FCSTD DOCUMENT  (FreeCAD 1.1R20260325 (Git shallow))
Label: FujiXE-design
License: Creative Commons Attribution 4.0
objects: Sketcher::SketchObject×9, Image::ImagePlane×4, App::Point×1, App::VarSet×1, PartDesign::Body×1
note: 19 computed .brp shape members not serialized (recipe doc carries the construction recipe); baked Part::Feature solids carry a one-line shape summary decoded from their .brp

FEATURE [App::Point] Origin001
  Role = Origin
FEATURE [App::VarSet] VarSet  label="Data"
  AVAngle = 38
  Height = 4.8
  MidGlyphWidth = 0.66
  MidHorizontalBarY = 2.2
  Thickness = 0.8
  ThinLetterWidth = 3.5
  TopOfA = 1
  Width = 3.95
FEATURE [Sketcher::SketchObject] Sketch  label="A"
  ArcFitTolerance = 1e-06
  AttachmentSupport = -> [Origin]
  ExternalTypes = [0]
  FullyConstrained = false
  MakeInternals = false
  MapMode = 5
  _ExternalGeoVersion = 1
  expr: Constraints[29] = <<Data>>.TopOfA
  expr: Constraints[30] = <<Data>>.AVAngle
  expr: Constraints[32] = <<Data>>.MidGlyphWidth
  expr: Constraints[36] = <<Data>>.Thickness
  expr: Constraints[37] = <<Data>>.Height
  sketch-geometry (17):
    g0: LineSegment StartX=23.478 StartY=44.0896 StartZ=0 EndX=25.1308 EndY=48.8896 EndZ=0
    g1: LineSegment StartX=25.1308 StartY=48.8896 StartZ=0 EndX=26.1308 EndY=48.8896 EndZ=0
    g2: LineSegment StartX=26.1308 StartY=48.8896 StartZ=0 EndX=27.7835 EndY=44.0896 EndZ=0
    g3: LineSegment StartX=27.7835 StartY=44.0896 StartZ=0 EndX=26.9374 EndY=44.0896 EndZ=0
    g4: LineSegment StartX=26.9374 StartY=44.0896 StartZ=0 EndX=26.5862 EndY=45.1096 EndZ=0
    g5: LineSegment StartX=26.5862 StartY=45.1096 StartZ=0 EndX=24.6753 EndY=45.1096 EndZ=0
    g6: LineSegment StartX=24.6753 StartY=45.1096 StartZ=0 EndX=24.3241 EndY=44.0896 EndZ=0
    g7: LineSegment StartX=24.3241 StartY=44.0896 StartZ=0 EndX=23.478 EndY=44.0896 EndZ=0
    g8: LineSegment StartX=24.9026 StartY=45.7696 StartZ=0 EndX=25.6308 EndY=47.8845 EndZ=0
    g9: LineSegment StartX=25.6308 StartY=47.8845 StartZ=0 EndX=26.359 EndY=45.7696 EndZ=0
    g10: LineSegment StartX=26.359 StartY=45.7696 StartZ=0 EndX=24.9026 EndY=45.7696 EndZ=0
    g11: GeomPoint [constr] X=25.6308 Y=45.7696 Z=0
    g12: GeomPoint [constr] X=25.6308 Y=48.8896 Z=0
    g13: LineSegment [constr] StartX=24.6753 StartY=45.1096 StartZ=0 EndX=23.9189 EndY=45.37 EndZ=0
    g14: GeomPoint [constr] X=25.6308 Y=45.1096 Z=0
    g15: GeomPoint [constr] X=25.6308 Y=44.0896 Z=0
    g16: GeomPoint [constr] X=25.6308 Y=45.4396 Z=0
  constraints (39):
    c: Coincident(g0,g1)
    c: Horizontal(g1)
    c: Coincident(g1,g2)
    c: Coincident(g2,g3)
    c: Horizontal(g3)
    c: Coincident(g3,g4)
    c: Coincident(g4,g5)
    c: Horizontal(g5)
    c: Coincident(g5,g6)
    c: Coincident(g6,g7)
    c: Coincident(g7,g0)
    c: Horizontal(g7)
    c: Horizontal(g6,g3)
    c: Coincident(g8,g9)
    c: Coincident(g9,g10)
    c: Coincident(g10,g8)
    c: Horizontal(g10)
    c: PointOnObject(g4,g9)
    c: PointOnObject(g5,g8)
    c: Parallel(g0,g6)
    c: Parallel(g4,g2)
    c: Symmetric(g10,g10,g11)
    c: Vertical(g8,g11)
    c: Symmetric(g1,g1,g12)
    c: Vertical(g8,g12)
    c: Equal(g7,g3)
    c: Coincident(g13,g5)
    c: PointOnObject(g13,g0)
    c: Perpendicular(g0,g13)
    c: DistanceX(g1,g1) = 1
    c: Angle(g0,g2) = 0.663225
    c: Symmetric(g5,g5,g14)
    c: DistanceY(g14,g11) = 0.66
    c: Symmetric(g6,g3,g15)
    c: Symmetric(g11,g14,g16)
    c: DistanceY(g15,g16) = 1.35
    c: Distance(g13) = 0.8
    c: DistanceY(g2,g1) = 4.8
    c: Parallel(g0,g8)
FEATURE [Sketcher::SketchObject] Sketch001  label="S"
  ArcFitTolerance = 1e-06
  AttachmentSupport = -> [Sketch]
  ExternalTypes = [0]
  FullyConstrained = false
  MakeInternals = false
  MapMode = 2
  _ExternalGeoVersion = 1
  sketch-geometry (50):
    g0: LineSegment StartX=8.4208 StartY=47.4982 StartZ=0 EndX=9.33017 EndY=47.532 EndZ=0
    g1: LineSegment StartX=5.53142 StartY=45.4144 StartZ=0 EndX=6.4408 EndY=45.4482 EndZ=0
    g2-g12: Circle [constr] x11 (B-spline internal-alignment scaffolding for g13; pole/knot coordinates omitted)
    g13: BSplineCurve PolesCount=11 KnotsCount=9 Degree=3 IsPeriodic=0
    g14-g22: GeomPoint [constr] x9 (B-spline internal-alignment scaffolding for g13; pole/knot coordinates omitted)
    g23-g36: Circle [constr] x14 (B-spline internal-alignment scaffolding for g37; pole/knot coordinates omitted)
    g37: BSplineCurve PolesCount=14 KnotsCount=12 Degree=3 IsPeriodic=0
    g38-g49: GeomPoint [constr] x12 (B-spline internal-alignment scaffolding for g37; pole/knot coordinates omitted)
  constraints (37):
    c: DistanceY(g1,g0) = 2.05
    c: DistanceX(g1,g0) = 1.98
    c: Equal(g1,g0)
    c: Parallel(g1,g0)
    c: Weight(g2) = 1
    c: Equal(g2, g3-g12) x10
    c: InternalAlignment(g2-g12 -> g13) x11
    c: InternalAlignment(g14-g22 -> g13) x9
    c: Coincident(g2,g0)
    c: Coincident(g12,g1)
    c: Horizontal(g19,g8)
    c: Vertical(g10,g21)
    c: DistanceY(g18,g0) = 0.91
    c: DistanceX(g18,g0) = 0.61
    c: DistanceX(g17,g0) = 2.19
    c: DistanceY(g17,g0) = 0.55
    c: DistanceX(g16,g13) = 1.82
    c: DistanceY(g13,g16) = 0.11
    c: DistanceY(g0,g3) = 0.55
    c: DistanceX(g3,g0) = 1
    c: DistanceY(g0,g15) = 0.64
    c: DistanceX(g15,g0) = 1.99
    c: DistanceY(g20,g0) = 3.2
    c: DistanceX(g20,g0) = 0.46
    c: DistanceX(g21,g0) = 2.21
    c: DistanceY(g21,g0) = 3.61
    c: DistanceY(g19,g0) = 2.01
    c: DistanceX(g0,g19) = 0.12
    c: Distance(g0) = 0.91
    c: Weight(g23) = 1
    c: Equal(g23, g24-g36) x13
    c: InternalAlignment(g23-g36 -> g37) x14
    c: InternalAlignment(g38-g49 -> g37) x12
    c: Coincident(g23,g0)
    c: PointOnObject(g25,g24)
    c: PointOnObject(g28,g27)
    c: Coincident(g36,g1)
FEATURE [Sketcher::SketchObject] Sketch002  label="Z"
  ArcFitTolerance = 1e-06
  AttachmentSupport = -> [Origin]
  ExternalTypes = [0]
  FullyConstrained = false
  MakeInternals = false
  MapMode = 5
  _ExternalGeoVersion = 1
  expr: Constraints[20] = <<Data>>.Height
  expr: Constraints[24] = <<Data>>.Width
  expr: Constraints[29] = <<Data>>.Thickness
  sketch-geometry (11):
    g0: LineSegment StartX=-9.16198 StartY=26.3031 StartZ=0 EndX=-9.16198 EndY=27.1031 EndZ=0
    g1: LineSegment StartX=-9.16198 StartY=27.1031 StartZ=0 EndX=-5.21198 EndY=27.1031 EndZ=0
    g2: LineSegment StartX=-5.21198 StartY=27.1031 StartZ=0 EndX=-5.21198 EndY=26.3031 EndZ=0
    g3: LineSegment StartX=-5.21198 StartY=26.3031 StartZ=0 EndX=-7.97324 EndY=23.1031 EndZ=0
    g4: LineSegment StartX=-7.97324 StartY=23.1031 StartZ=0 EndX=-5.21198 EndY=23.1031 EndZ=0
    g5: LineSegment StartX=-5.21198 StartY=23.1031 StartZ=0 EndX=-5.21198 EndY=22.3031 EndZ=0
    g6: LineSegment StartX=-5.21198 StartY=22.3031 StartZ=0 EndX=-9.16198 EndY=22.3031 EndZ=0
    g7: LineSegment StartX=-9.16198 StartY=22.3031 StartZ=0 EndX=-9.16198 EndY=23.1031 EndZ=0
    g8: LineSegment StartX=-9.16198 StartY=23.1031 StartZ=0 EndX=-6.40072 EndY=26.3031 EndZ=0
    g9: LineSegment StartX=-6.40072 StartY=26.3031 StartZ=0 EndX=-9.16198 EndY=26.3031 EndZ=0
    g10: LineSegment [constr] StartX=-7.97324 StartY=23.1031 StartZ=0 EndX=-8.65463 EndY=23.6911 EndZ=0
  constraints (31):
    c: Vertical(g0)
    c: Coincident(g0,g1)
    c: Horizontal(g1)
    c: Coincident(g1,g2)
    c: Vertical(g2)
    c: Coincident(g2,g3)
    c: Coincident(g3,g4)
    c: Horizontal(g4)
    c: Coincident(g4,g5)
    c: Vertical(g5)
    c: Coincident(g5,g6)
    c: Horizontal(g6)
    c: Coincident(g6,g7)
    c: Vertical(g7)
    c: Coincident(g7,g8)
    c: Coincident(g8,g9)
    c: Coincident(g9,g0)
    c: Horizontal(g9)
    c: Vertical(g2,g4)
    c: Vertical(g0,g7)
    c: DistanceY(g6,g0) = 4.8
    c: Horizontal(g8,g2)
    c: Horizontal(g7,g3)
    c: Parallel(g8,g3)
    c: DistanceX(g6,g6) = 3.95
    c: Coincident(g10,g3)
    c: PointOnObject(g10,g8)
    c: Perpendicular(g8,g10)
    c: Distance(g10) = 0.9
    c: DistanceY(g5,g5) = 0.8
    c: Equal(g5,g0)
FEATURE [Sketcher::SketchObject] Sketch003  label="X"
  ArcFitTolerance = 1e-06
  AttachmentSupport = -> [Sketch002]
  ExternalTypes = [0]
  FullyConstrained = false
  MakeInternals = false
  MapMode = 2
  _ExternalGeoVersion = 1
  expr: Constraints[16] = <<Data>>.Height
  sketch-geometry (13):
    g0: LineSegment StartX=8.97005 StartY=27.4466 StartZ=0 EndX=9.9513 EndY=27.4466 EndZ=0
    g1: LineSegment StartX=9.9513 StartY=27.4466 StartZ=0 EndX=10.8301 EndY=25.9184 EndZ=0
    g2: LineSegment StartX=10.8301 StartY=25.9184 StartZ=0 EndX=11.7088 EndY=27.4466 EndZ=0
    g3: LineSegment StartX=11.7088 StartY=27.4466 StartZ=0 EndX=12.6901 EndY=27.4466 EndZ=0
    g4: LineSegment StartX=12.6901 StartY=27.4466 StartZ=0 EndX=11.3801 EndY=25.1684 EndZ=0
    g5: LineSegment StartX=11.3801 StartY=25.1684 StartZ=0 EndX=12.8301 EndY=22.6466 EndZ=0
    g6: LineSegment StartX=12.8301 StartY=22.6466 StartZ=0 EndX=11.8488 EndY=22.6466 EndZ=0
    g7: LineSegment StartX=11.8488 StartY=22.6466 StartZ=0 EndX=10.8301 EndY=24.4184 EndZ=0
    g8: LineSegment StartX=10.8301 StartY=24.4184 StartZ=0 EndX=9.8113 EndY=22.6466 EndZ=0
    g9: LineSegment StartX=9.8113 StartY=22.6466 StartZ=0 EndX=8.83005 EndY=22.6466 EndZ=0
    g10: LineSegment StartX=8.83005 StartY=22.6466 StartZ=0 EndX=10.2801 EndY=25.1684 EndZ=0
    g11: LineSegment StartX=10.2801 StartY=25.1684 StartZ=0 EndX=8.97005 EndY=27.4466 EndZ=0
    g12: LineSegment [constr] StartX=10.8301 StartY=24.4184 StartZ=0 EndX=10.8301 EndY=25.9184 EndZ=0
  constraints (33):
    c: Horizontal(g0)
    c: Coincident(g0,g1)
    c: Coincident(g1,g2)
    c: Coincident(g2,g3)
    c: Horizontal(g3)
    c: Coincident(g3,g4)
    c: Coincident(g4,g5)
    c: Coincident(g5,g6)
    c: Horizontal(g6)
    c: Coincident(g6,g7)
    c: Coincident(g7,g8)
    c: Coincident(g8,g9)
    c: Horizontal(g9)
    c: Coincident(g9,g10)
    c: Coincident(g10,g11)
    c: Coincident(g11,g0)
    c: DistanceY(g9,g0) = 4.8
    c: Horizontal(g10,g4)
    c: Coincident(g12,g7)
    c: Coincident(g12,g1)
    c: Symmetric(g0,g2,g12)
    c: Symmetric(g8,g6,g12)
    c: Equal(g0,g3)
    c: Equal(g9,g6)
    c: Parallel(g10,g8)
    c: Parallel(g11,g1)
    c: Symmetric(g10,g4,g12)
    c: Parallel(g10,g2)
    c: DistanceX(g0,g3) = 3.72
    c: DistanceX(g9,g5) = 4
    c: DistanceX(g10,g4) = 1.1
    c: DistanceY(g12,g12) = 1.5
    c: Equal(g9,g3)
FEATURE [Sketcher::SketchObject] Sketch004  label="Q"
  ArcFitTolerance = 1e-06
  AttachmentSupport = -> [Origin]
  ExternalTypes = [0]
  FullyConstrained = false
  MakeInternals = false
  MapMode = 5
  _ExternalGeoVersion = 1
  sketch-geometry (19):
    g0: ArcOfEllipse CenterX=1.09175 CenterY=89.324 CenterZ=0 NormalX=0 NormalY=0 NormalZ=1 MajorRadius=1.75 MinorRadius=1.35 AngleXU=-1.5708 StartAngle=0.938881 EndAngle=6.76111
    g1: LineSegment [constr] StartX=1.09175 StartY=87.574 StartZ=0 EndX=1.09175 EndY=91.074 EndZ=0
    g2: LineSegment [constr] StartX=2.44175 StartY=89.324 StartZ=0 EndX=-0.258249 EndY=89.324 EndZ=0
    g3: GeomPoint [constr] X=1.09175 Y=88.2105 Z=0
    g4: GeomPoint [constr] X=1.09175 Y=90.4376 Z=0
    g5: ArcOfEllipse CenterX=1.09175 CenterY=89.324 CenterZ=0 NormalX=0 NormalY=0 NormalZ=1 MajorRadius=2.5 MinorRadius=2.25 AngleXU=-1.5708 StartAngle=0.873331 EndAngle=6.85864
    g6: LineSegment [constr] StartX=1.09175 StartY=86.824 StartZ=0 EndX=1.09175 EndY=91.824 EndZ=0
    g7: LineSegment [constr] StartX=3.34175 StartY=89.324 StartZ=0 EndX=-1.15825 EndY=89.324 EndZ=0
    g8: GeomPoint [constr] X=1.09175 Y=88.2343 Z=0
    g9: GeomPoint [constr] X=1.09175 Y=90.4138 Z=0
    g10: LineSegment StartX=2.18106 StartY=88.2903 StartZ=0 EndX=1.77233 EndY=88.6583 EndZ=0
    g11: LineSegment StartX=1.77233 StartY=88.6583 StartZ=0 EndX=1.30394 EndY=88.1381 EndZ=0
    g12: LineSegment StartX=1.30394 StartY=88.1381 StartZ=0 EndX=1.71267 EndY=87.7701 EndZ=0
    g13: LineSegment StartX=2.31624 StartY=87.2267 StartZ=0 EndX=2.86812 EndY=86.7297 EndZ=0
    g14: LineSegment StartX=2.86812 StartY=86.7297 StartZ=0 EndX=3.33652 EndY=87.2499 EndZ=0
    g15: LineSegment StartX=3.33652 StartY=87.2499 StartZ=0 EndX=2.81631 EndY=87.7183 EndZ=0
    g16: GeomPoint [constr] X=1.53814 Y=88.3982 Z=0
    g17: GeomPoint [constr] X=3.10232 Y=86.9898 Z=0
    g18: LineSegment [constr] StartX=1.53814 StartY=88.3982 StartZ=0 EndX=3.10232 EndY=86.9898 EndZ=0
  constraints (32):
    c: InternalAlignment(g1-g4 -> g0) x4
    c: Vertical(g1)
    c: DistanceY(g1,g1) = 3.5
    c: DistanceX(g2,g2) = 2.7
    c: InternalAlignment(g6-g9 -> g5) x4
    c: Coincident(g5,g0)
    c: Coincident(g10,g0)
    c: Coincident(g10,g11)
    c: Coincident(g11,g12)
    c: Coincident(g12,g0)
    c: Coincident(g13,g5)
    c: Coincident(g13,g14)
    c: Coincident(g14,g15)
    c: Coincident(g15,g5)
    c: Parallel(g12,g10)
    c: Parallel(g13,g15)
    c: Parallel(g10,g15)
    c: Horizontal(g7)
    c: DistanceX(g7,g2) = 0.9
    c: DistanceY(g6,g1) = 0.75
    c: Symmetric(g11,g11,g16)
    c: Symmetric(g14,g14,g17)
    c: Coincident(g18,g16)
    c: Coincident(g18,g17)
    c: Symmetric(g0,g0,g18)
    c: Perpendicular(g10,g11)
    c: Perpendicular(g14,g15)
    c: Equal(g11,g14)
    c: Angle(g1,g18) = 0.837758
    c: Distance(g10) = 0.55
    c: Distance(g15) = 0.7
    c: Distance(g14) = 0.7
FEATURE [Sketcher::SketchObject] Sketch005  label="W"
  ArcFitTolerance = 1e-06
  AttachmentSupport = -> [Sketch004,XY_Plane]
  ExternalTypes = [0]
  FullyConstrained = false
  MakeInternals = false
  MapMode = 2
  _ExternalGeoVersion = 1
  expr: Constraints[21] = <<Data>>.Height
  expr: Constraints[39] = <<Data>>.Thickness
  sketch-geometry (17):
    g0: LineSegment StartX=16.8181 StartY=91.9053 StartZ=0 EndX=18.1042 EndY=87.1053 EndZ=0
    g1: LineSegment StartX=18.1042 StartY=87.1053 StartZ=0 EndX=19.04 EndY=87.1053 EndZ=0
    g2: LineSegment StartX=19.04 StartY=87.1053 StartZ=0 EndX=19.8181 EndY=90.4753 EndZ=0
    g3: LineSegment StartX=19.8181 StartY=90.4753 StartZ=0 EndX=20.5961 EndY=87.1053 EndZ=0
    g4: LineSegment StartX=20.5961 StartY=87.1053 StartZ=0 EndX=21.5319 EndY=87.1053 EndZ=0
    g5: LineSegment StartX=21.5319 StartY=87.1053 StartZ=0 EndX=22.8181 EndY=91.9053 EndZ=0
    g6: LineSegment StartX=22.8181 StartY=91.9053 StartZ=0 EndX=21.9898 EndY=91.9053 EndZ=0
    g7: LineSegment StartX=21.9898 StartY=91.9053 StartZ=0 EndX=21.0596 EndY=88.4335 EndZ=0
    g8: LineSegment StartX=21.0596 StartY=88.4335 StartZ=0 EndX=20.2581 EndY=91.9053 EndZ=0
    g9: LineSegment StartX=20.2581 StartY=91.9053 StartZ=0 EndX=19.3781 EndY=91.9053 EndZ=0
    g10: LineSegment StartX=19.3781 StartY=91.9053 StartZ=0 EndX=18.5765 EndY=88.4335 EndZ=0
    g11: LineSegment StartX=18.5765 StartY=88.4335 StartZ=0 EndX=17.6463 EndY=91.9053 EndZ=0
    g12: LineSegment StartX=17.6463 StartY=91.9053 StartZ=0 EndX=16.8181 EndY=91.9053 EndZ=0
    g13: LineSegment [constr] StartX=19.8181 StartY=87.1053 StartZ=0 EndX=19.8181 EndY=91.9053 EndZ=0
    g14: LineSegment [constr] StartX=18.5721 StartY=87.1053 StartZ=0 EndX=18.5765 EndY=88.4335 EndZ=0
    g15: LineSegment [constr] StartX=21.064 StartY=87.1053 StartZ=0 EndX=21.0596 EndY=88.4335 EndZ=0
    g16: LineSegment [constr] StartX=18.5765 StartY=88.4335 StartZ=0 EndX=17.8038 EndY=88.2265 EndZ=0
  constraints (45):
    c: Coincident(g0,g1)
    c: Coincident(g1,g2)
    c: Coincident(g2,g3)
    c: Coincident(g3,g4)
    c: Horizontal(g4)
    c: Coincident(g4,g5)
    c: Coincident(g5,g6)
    c: Horizontal(g6)
    c: Coincident(g6,g7)
    c: Coincident(g7,g8)
    c: Coincident(g8,g9)
    c: Coincident(g9,g10)
    c: Coincident(g10,g11)
    c: Coincident(g11,g12)
    c: Coincident(g12,g0)
    c: Horizontal(g6,g8)
    c: Horizontal(g3,g1)
    c: Symmetric(g9,g9,g13)
    c: Vertical(g13)
    c: Symmetric(g1,g3,g13)
    c: PointOnObject(g2,g13)
    c: DistanceY(g0,g0) = 4.8
    c: Parallel(g0,g11)
    c: Parallel(g10,g2)
    c: Parallel(g3,g8)
    c: Parallel(g7,g5)
    c: Equal(g1,g4)
    c: Symmetric(g1,g1,g14)
    c: Coincident(g14,g10)
    c: Symmetric(g4,g4,g15)
    c: Coincident(g15,g7)
    c: Coincident(g16,g10)
    c: PointOnObject(g16,g0)
    c: Perpendicular(g0,g16)
    c: Horizontal(g1)
    c: Angle(g2,g3) = 0.453786
    c: Angle(g10,g11) = 0.488692
    c: Horizontal(g12)
    c: Horizontal(g9)
    c: Distance(g16) = 0.8
    c: DistanceX(g0,g5) = 6
    c: Symmetric(g11,g6,g13)
    c: Angle(g7,g8) = 0.488692
    c: DistanceX(g9,g9) = 0.88
    c: DistanceY(g13,g2) = 3.37
FEATURE [Sketcher::SketchObject] Sketch006  label="E"
  ArcFitTolerance = 1e-06
  AttachmentSupport = -> [Origin]
  ExternalTypes = [0]
  FullyConstrained = false
  MakeInternals = false
  MapMode = 5
  _ExternalGeoVersion = 1
  expr: Constraints[26] = <<Data>>.Height
  expr: Constraints[32] = <<Data>>.ThinLetterWidth
  expr: Constraints[33] = <<Data>>.MidHorizontalBarY
  sketch-geometry (12):
    g0: LineSegment StartX=38.8647 StartY=91.9226 StartZ=0 EndX=35.3647 EndY=91.9226 EndZ=0
    g1: LineSegment StartX=35.3647 StartY=91.9226 StartZ=0 EndX=35.3647 EndY=87.1226 EndZ=0
    g2: LineSegment StartX=35.3647 StartY=87.1226 StartZ=0 EndX=38.8647 EndY=87.1226 EndZ=0
    g3: LineSegment StartX=38.8647 StartY=87.1226 StartZ=0 EndX=38.8647 EndY=87.8226 EndZ=0
    g4: LineSegment StartX=38.8647 StartY=87.8226 StartZ=0 EndX=36.2147 EndY=87.8226 EndZ=0
    g5: LineSegment StartX=36.2147 StartY=87.8226 StartZ=0 EndX=36.2147 EndY=89.3226 EndZ=0
    g6: LineSegment StartX=36.2147 StartY=89.3226 StartZ=0 EndX=38.5647 EndY=89.3226 EndZ=0
    g7: LineSegment StartX=38.5647 StartY=89.3226 StartZ=0 EndX=38.5647 EndY=90.0226 EndZ=0
    g8: LineSegment StartX=38.5647 StartY=90.0226 StartZ=0 EndX=36.2147 EndY=90.0226 EndZ=0
    g9: LineSegment StartX=36.2147 StartY=90.0226 StartZ=0 EndX=36.2147 EndY=91.2226 EndZ=0
    g10: LineSegment StartX=36.2147 StartY=91.2226 StartZ=0 EndX=38.8647 EndY=91.2226 EndZ=0
    g11: LineSegment StartX=38.8647 StartY=91.2226 StartZ=0 EndX=38.8647 EndY=91.9226 EndZ=0
  constraints (34):
    c: Horizontal(g0)
    c: Coincident(g0,g1)
    c: Vertical(g1)
    c: Coincident(g1,g2)
    c: Horizontal(g2)
    c: Coincident(g2,g3)
    c: Vertical(g3)
    c: Coincident(g3,g4)
    c: Horizontal(g4)
    c: Coincident(g4,g5)
    c: Vertical(g5)
    c: Coincident(g5,g6)
    c: Horizontal(g6)
    c: Coincident(g6,g7)
    c: Vertical(g7)
    c: Coincident(g7,g8)
    c: Horizontal(g8)
    c: Coincident(g8,g9)
    c: Vertical(g9)
    c: Coincident(g9,g10)
    c: Horizontal(g10)
    c: Coincident(g10,g11)
    c: Coincident(g11,g0)
    c: Vertical(g11)
    c: Equal(g3,g11)
    c: Vertical(g3,g10)
    c: DistanceY(g1,g1) = 4.8
    c: Vertical(g8,g5)
    c: DistanceX(g1,g4) = 0.85
    c: DistanceY(g11,g11) = 0.7
    c: Equal(g7,g11)
    c: DistanceX(g6,g6) = 2.35
    c: DistanceX(g2,g2) = 3.5
    c: DistanceY(g1,g5) = 2.2
FEATURE [Image::ImagePlane] Atari_XE_row_1_caps_reference  label="Atari XE row 1 caps reference"
  XSize = 170.541
  YSize = 65.9345
FEATURE [Image::ImagePlane] Atari_XE_row_2_caps_reference  label="Atari XE row 2 caps reference"
  Placement = pos=(0,46.43,0) rot=(0,0,1;0rad)
  XSize = 141.775
  YSize = 48.4929
FEATURE [Image::ImagePlane] Atari_XE_row_3_caps_reference  label="Atari XE row 3 caps reference"
  Placement = pos=(0,89.74,0) rot=(0,0,1;0rad)
  XSize = 139.065
  YSize = 48.4506
FEATURE [Image::ImagePlane] Atari_XE_row_4_caps_reference  label="Atari XE row 4 caps reference"
  Placement = pos=(0,141.549,0) rot=(0,0,1;0rad)
  XSize = 146.114
  YSize = 55.3298
FEATURE [Sketcher::SketchObject] Sketch007  label="O"
  ArcFitTolerance = 1e-06
  AttachmentSupport = -> [Origin]
  ExternalTypes = [0]
  FullyConstrained = false
  MakeInternals = false
  MapMode = 5
  _ExternalGeoVersion = 1
  sketch-geometry (10):
    g0: Ellipse CenterX=55.1305 CenterY=107.248 CenterZ=0 NormalX=0 NormalY=0 NormalZ=1 MajorRadius=1.74 MinorRadius=1.325 AngleXU=1.5708
    g1: LineSegment [constr] StartX=55.1305 StartY=108.988 StartZ=0 EndX=55.1305 EndY=105.508 EndZ=0
    g2: LineSegment [constr] StartX=53.8055 StartY=107.248 StartZ=0 EndX=56.4555 EndY=107.248 EndZ=0
    g3: GeomPoint [constr] X=55.1305 Y=108.376 Z=0
    g4: GeomPoint [constr] X=55.1305 Y=106.121 Z=0
    g5: Ellipse CenterX=55.1305 CenterY=107.248 CenterZ=0 NormalX=0 NormalY=0 NormalZ=1 MajorRadius=2.5 MinorRadius=2.25 AngleXU=1.5708
    g6: LineSegment [constr] StartX=55.1305 StartY=109.748 StartZ=0 EndX=55.1305 EndY=104.748 EndZ=0
    g7: LineSegment [constr] StartX=52.8805 StartY=107.248 StartZ=0 EndX=57.3805 EndY=107.248 EndZ=0
    g8: GeomPoint [constr] X=55.1305 Y=108.338 Z=0
    g9: GeomPoint [constr] X=55.1305 Y=106.159 Z=0
  constraints (9):
    c: InternalAlignment(g1-g4 -> g0) x4
    c: InternalAlignment(g6-g9 -> g5) x4
    c: Coincident(g5,g0)
    c: DistanceY(g1,g1) = 3.48
    c: Horizontal(g7)
    c: DistanceX(g7,g7) = 4.5
    c: DistanceY(g6,g6) = 5
    c: DistanceX(g2,g2) = 2.65
    c: Horizontal(g2)
FEATURE [Sketcher::SketchObject] Sketch008  label="Esc"
  ArcFitTolerance = 1e-06
  AttachmentSupport = -> [Origin]
  ExternalTypes = [0]
  FullyConstrained = false
  MakeInternals = false
  MapMode = 5
  _ExternalGeoVersion = 1
  sketch-geometry (100):
    g0: LineSegment StartX=-30.1712 StartY=151.764 StartZ=0 EndX=-32.0212 EndY=151.764 EndZ=0
    g1: LineSegment StartX=-32.0212 StartY=151.764 StartZ=0 EndX=-32.0212 EndY=149.264 EndZ=0
    g2: LineSegment StartX=-32.0212 StartY=149.264 StartZ=0 EndX=-30.1712 EndY=149.264 EndZ=0
    g3: LineSegment StartX=-30.1712 StartY=149.264 StartZ=0 EndX=-30.1712 EndY=149.664 EndZ=0
    g4: LineSegment StartX=-30.1712 StartY=149.664 StartZ=0 EndX=-31.5212 EndY=149.664 EndZ=0
    g5: LineSegment StartX=-31.5212 StartY=149.664 StartZ=0 EndX=-31.5212 EndY=150.364 EndZ=0
    g6: LineSegment StartX=-31.5212 StartY=150.364 StartZ=0 EndX=-30.3712 EndY=150.364 EndZ=0
    g7: LineSegment StartX=-30.3712 StartY=150.364 StartZ=0 EndX=-30.3712 EndY=150.764 EndZ=0
    g8: LineSegment StartX=-30.3712 StartY=150.764 StartZ=0 EndX=-31.5212 EndY=150.764 EndZ=0
    g9: LineSegment StartX=-31.5212 StartY=150.764 StartZ=0 EndX=-31.5212 EndY=151.364 EndZ=0
    g10: LineSegment StartX=-31.5212 StartY=151.364 StartZ=0 EndX=-30.1712 EndY=151.364 EndZ=0
    g11: LineSegment StartX=-30.1712 StartY=151.364 StartZ=0 EndX=-30.1712 EndY=151.764 EndZ=0
    g12: LineSegment StartX=-28.7191 StartY=150.664 StartZ=0 EndX=-28.3898 EndY=150.745 EndZ=0
    g13: LineSegment StartX=-29.8033 StartY=149.651 StartZ=0 EndX=-29.474 EndY=149.732 EndZ=0
    g14-g26: GeomPoint [constr] x13 (B-spline internal-alignment scaffolding for g27; pole/knot coordinates omitted)
    g27: BSplineCurve PolesCount=15 KnotsCount=13 Degree=3 IsPeriodic=0
    g28-g42: Circle [constr] x15 (B-spline internal-alignment scaffolding for g27; pole/knot coordinates omitted)
    g43-g55: GeomPoint [constr] x13 (B-spline internal-alignment scaffolding for g56; pole/knot coordinates omitted)
    g56: BSplineCurve PolesCount=15 KnotsCount=13 Degree=3 IsPeriodic=0
    g57-g71: Circle [constr] x15 (B-spline internal-alignment scaffolding for g56; pole/knot coordinates omitted)
    g72: LineSegment StartX=-26.6064 StartY=150.454 StartZ=0 EndX=-26.2064 EndY=150.478 EndZ=0
    g73: LineSegment StartX=-26.6095 StartY=149.785 StartZ=0 EndX=-26.207 EndY=149.804 EndZ=0
    g74: ArcOfEllipse CenterX=-27.0485 CenterY=150.144 CenterZ=0 NormalX=0 NormalY=0 NormalZ=1 MajorRadius=0.95819 MinorRadius=0.899145 AngleXU=-1.5552 StartAngle=1.9123 EndAngle=7.47727
    g75: LineSegment [constr] StartX=-27.0335 StartY=149.185 StartZ=0 EndX=-27.0634 EndY=151.102 EndZ=0
    g76: LineSegment [constr] StartX=-26.1494 StartY=150.158 StartZ=0 EndX=-27.9475 EndY=150.13 EndZ=0
    g77: GeomPoint [constr] X=-27.0433 Y=149.812 Z=0
    g78: GeomPoint [constr] X=-27.0536 Y=150.475 Z=0
    g79-g87: GeomPoint [constr] x9 (B-spline internal-alignment scaffolding for g88; pole/knot coordinates omitted)
    g88: BSplineCurve PolesCount=11 KnotsCount=9 Degree=3 IsPeriodic=0
    g89-g99: Circle [constr] x11 (B-spline internal-alignment scaffolding for g88; pole/knot coordinates omitted)
  constraints (136):
    c: Horizontal(g0)
    c: Coincident(g0,g1)
    c: Vertical(g1)
    c: Coincident(g1,g2)
    c: Horizontal(g2)
    c: Coincident(g2,g3)
    c: Vertical(g3)
    c: Coincident(g3,g4)
    c: Horizontal(g4)
    c: Coincident(g4,g5)
    c: Vertical(g5)
    c: Coincident(g5,g6)
    c: Horizontal(g6)
    c: Coincident(g6,g7)
    c: Vertical(g7)
    c: Coincident(g7,g8)
    c: Horizontal(g8)
    c: Coincident(g8,g9)
    c: Vertical(g9)
    c: Coincident(g9,g10)
    c: Horizontal(g10)
    c: Coincident(g10,g11)
    c: Coincident(g11,g0)
    c: Vertical(g11)
    c: Vertical(g8,g5)
    c: Vertical(g10,g3)
    c: Equal(g11,g3)
    c: DistanceY(g1,g1) = 2.5
    c: DistanceX(g0,g0) = 1.85
    c: DistanceY(g9,g9) = 0.6
    c: DistanceY(g5,g5) = 0.7
    c: DistanceY(g11,g11) = 0.4
    c: DistanceX(g1,g4) = 0.5
    c: DistanceX(g6,g6) = 1.15
    c: Parallel(g13,g12)
    c: Equal(g13,g12)
    c: InternalAlignment(g14-g26 -> g27) x13
    c: InternalAlignment(g28,g27)
    c: Weight(g28) = 1
    c: InternalAlignment(g29,g27)
    c: Equal(g29,g28)
    c: InternalAlignment(g30,g27)
    c: Equal(g30,g28)
    c: InternalAlignment(g31,g27)
    c: Equal(g31,g28)
    c: InternalAlignment(g32,g27)
    c: Equal(g32,g28)
    c: InternalAlignment(g33,g27)
    c: Equal(g33,g28)
    c: InternalAlignment(g34,g27)
    c: Equal(g34,g28)
    c: InternalAlignment(g35,g27)
    c: Equal(g35,g28)
    c: InternalAlignment(g36,g27)
    c: Equal(g36,g28)
    c: InternalAlignment(g37,g27)
    c: Equal(g37,g28)
    c: InternalAlignment(g38,g27)
    c: Equal(g38,g28)
    c: InternalAlignment(g39,g27)
    c: Equal(g39,g28)
    c: InternalAlignment(g40,g27)
    c: Equal(g40,g28)
    c: InternalAlignment(g41,g27)
    c: Equal(g41,g28)
    c: InternalAlignment(g42,g27)
    c: Equal(g42,g28)
    c: Coincident(g14,g12)
    c: Coincident(g26,g13)
    c: InternalAlignment(g43-g55 -> g56) x13
    c: InternalAlignment(g57,g56)
    c: Weight(g57) = 1
    c: InternalAlignment(g58,g56)
    c: Equal(g58,g57)
    c: InternalAlignment(g59,g56)
    c: Equal(g59,g57)
    c: InternalAlignment(g60,g56)
    c: Equal(g60,g57)
    c: InternalAlignment(g61,g56)
    c: Equal(g61,g57)
    c: InternalAlignment(g62,g56)
    c: Equal(g62,g57)
    c: InternalAlignment(g63,g56)
    c: Equal(g63,g57)
    c: InternalAlignment(g64,g56)
    c: Equal(g64,g57)
    c: InternalAlignment(g65,g56)
    c: Equal(g65,g57)
    c: InternalAlignment(g66,g56)
    c: Equal(g66,g57)
    c: InternalAlignment(g67,g56)
    c: Equal(g67,g57)
    c: InternalAlignment(g68,g56)
    c: Equal(g68,g57)
    c: InternalAlignment(g69,g56)
    c: Equal(g69,g57)
    c: InternalAlignment(g70,g56)
    c: Equal(g70,g57)
    c: InternalAlignment(g71,g56)
    c: Equal(g71,g57)
    c: Coincident(g43,g13)
    c: Coincident(g55,g12)
    c: InternalAlignment(g75-g78 -> g74) x4
    c: Coincident(g74,g73)
    c: Coincident(g74,g72)
    c: Horizontal(g24,g75)
    c: Horizontal(g53,g75)
    c: Block(g74)
    c: InternalAlignment(g79-g87 -> g88) x9
    c: InternalAlignment(g89,g88)
    c: Weight(g89) = 1
    c: InternalAlignment(g90,g88)
    c: Equal(g90,g89)
    c: InternalAlignment(g91,g88)
    c: Equal(g91,g89)
    c: InternalAlignment(g92,g88)
    c: Equal(g92,g89)
    c: InternalAlignment(g93,g88)
    c: Equal(g93,g89)
    c: InternalAlignment(g94,g88)
    c: Equal(g94,g89)
    c: InternalAlignment(g95,g88)
    c: Equal(g95,g89)
    c: InternalAlignment(g96,g88)
    c: Equal(g96,g89)
    c: InternalAlignment(g97,g88)
    c: Equal(g97,g89)
    c: InternalAlignment(g98,g88)
    c: Equal(g98,g89)
    c: InternalAlignment(g99,g88)
    c: Equal(g99,g89)
    c: Coincident(g79,g72)
    c: PointOnObject(g81,g75)
    c: PointOnObject(g83,g76)
    c: PointOnObject(g85,g75)
    c: Coincident(g87,g73)
FEATURE [PartDesign::Body] Body
  AllowCompound = false
  Group = -> [VarSet,Sketch,Sketch006,Sketch007,Sketch004,Sketch001,Sketch005,Sketch003,Sketch002,Sketch008]
  Origin = -> Origin
